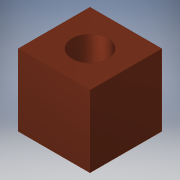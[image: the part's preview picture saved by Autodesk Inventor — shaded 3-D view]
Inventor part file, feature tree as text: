
AUTODESK INVENTOR PART (.ipt)
format: ipt  version: 2018 (Build 220112000, 112)  size: 93,184 bytes
history: native  units: in
note: dims shown in document units (in); Inventor stores cm internally (conversion verified against a paired STEP export)
features: extrude x1, sketch x1
ambient origin geometry x8: Origin, YZ Plane, XZ Plane, XY Plane, X Axis, Y Axis, Z Axis, Center Point
bodies: Solid1 (feature_tree)
feature tree (2):
  extrude  "Extrusion1"  Depth=1.0in
  sketch  "Sketch1"  dims[d0=0.5in d1=1.0in d2=1.0in d3=1.0in d4=0.0in]
